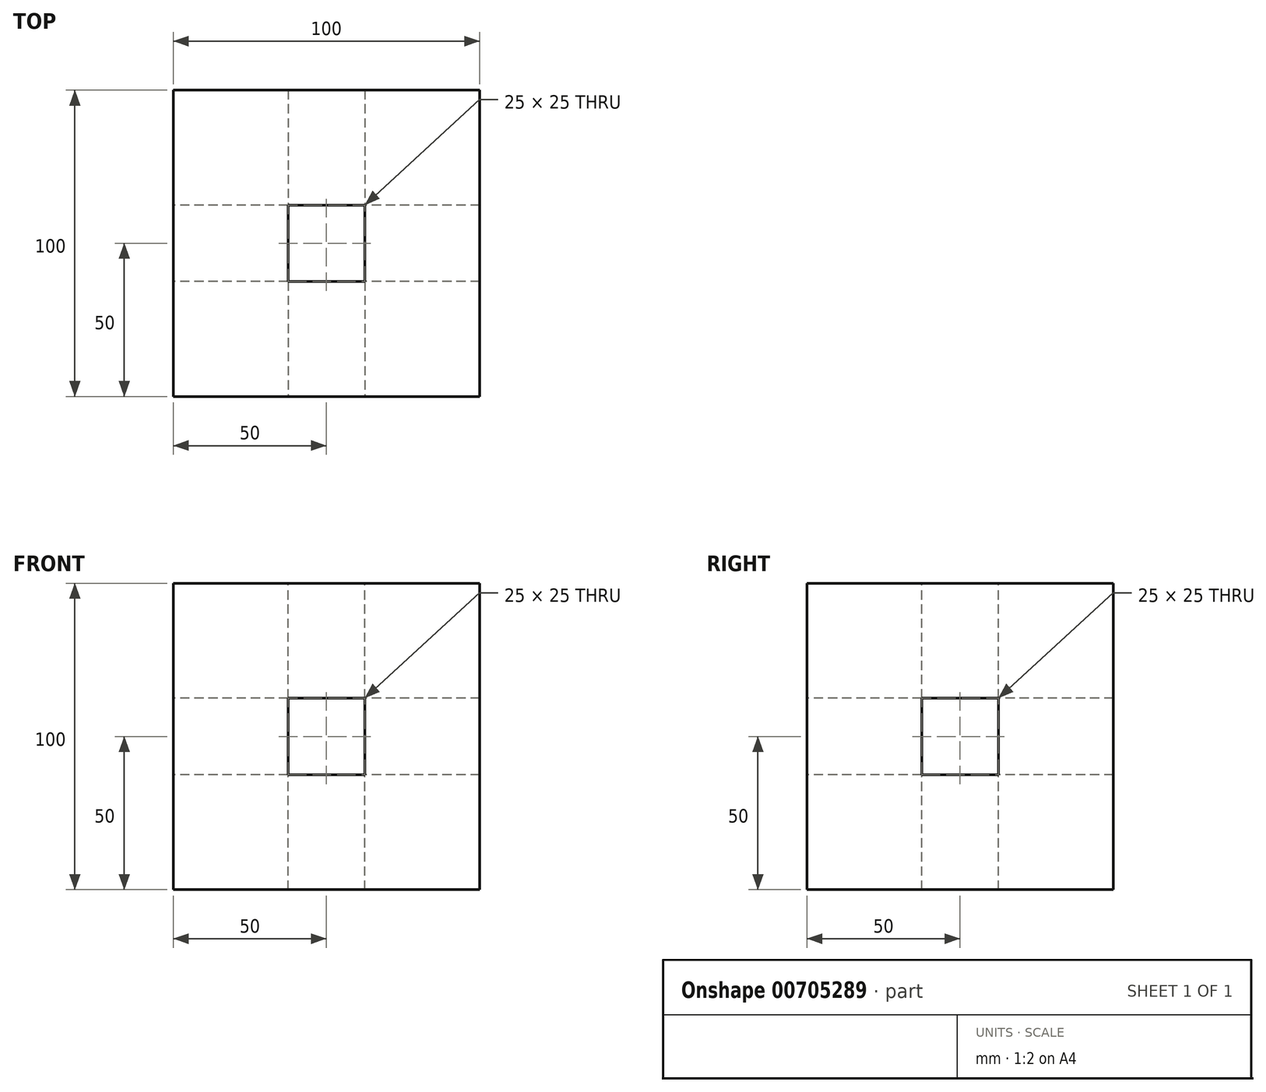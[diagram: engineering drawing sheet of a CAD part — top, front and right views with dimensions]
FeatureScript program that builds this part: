
annotation { "Feature Type Name" : "Feature", "Feature Type Description" : "" }
export const myFeature = defineFeature(function(context is Context, id is Id, definition is map)
    precondition{}
    {
        {
            var Q0;
            Q0=qCreatedBy(makeId("Top.planeOp"),FACE);
            var sketch = newSketch(context, id + "F0", { "sketchPlane" : qUnion([Q0])});
            skLineSegment(sketch, "E0.bottom", {"start": v(50, -50) * mm, "end": v(-50, -50) * mm});
            skLineSegment(sketch, "E0.top", {"start": v(50, 50) * mm, "end": v(-50, 50) * mm});
            skLineSegment(sketch, "E0.left", {"start": v(50, -50) * mm, "end": v(50, 50) * mm});
            skLineSegment(sketch, "E0.right", {"start": v(-50, -50) * mm, "end": v(-50, 50) * mm});
            skPoint(sketch, "E0.middle", {"position": v(0, 0) * mm});
            skSolve(sketch);
        }
        {
            var Q0;
            Q0=qSketchRegion(id+"F0",true);
            extrude(context, id + "F1", {"entities" : qUnion([Q0]), "depth" : 100 * mm, "offsetDistance" : 25 * mm});
        }
        {
            var Q0;
            Q0=makeQuery(id+"F1.opExtrude","SWEPT_FACE",FACE,{"disambiguationData":[OSD([sQuery(id+"F0.wireOp",EDGE,"E0.bottom")])]});
            var sketch = newSketch(context, id + "F2", { "sketchPlane" : qUnion([Q0])});
            skLineSegment(sketch, "E1.bottom", {"start": v(12.5, 37.5) * mm, "end": v(-12.5, 37.5) * mm});
            skLineSegment(sketch, "E1.top", {"start": v(12.5, 62.5) * mm, "end": v(-12.5, 62.5) * mm});
            skLineSegment(sketch, "E1.left", {"start": v(12.5, 37.5) * mm, "end": v(12.5, 62.5) * mm});
            skLineSegment(sketch, "E1.right", {"start": v(-12.5, 37.5) * mm, "end": v(-12.5, 62.5) * mm});
            skPoint(sketch, "E1.middle", {"position": v(0, 50) * mm});
            skPoint(sketch, "E1.middle.positionSnap0", {"position": v(-50, 50) * mm});
            skPoint(sketch, "E1.centerSnap0", {"position": v(-50, 50) * mm});
            skSolve(sketch);
        }
        {
            var Q0;
            Q0=makeQuery(id+"F2.imprint","IMPRINT",FACE,{"disambiguationData":[TD([[makeQuery(id+"F2.imprint","IMPRINT",EDGE,{"derivedFrom":sQuery(id+"F2.wireOp",EDGE,"E1.bottom")}),-1.0]])]});
            extrude(context, id + "F3", {"entities" : qUnion([Q0]), "operationType" : NewBodyOperationType.REMOVE, "endBound" : BoundingType.THROUGH_ALL, "oppositeDirection" : true, "depth" : 25 * mm, "offsetDistance" : 25 * mm});
        }
        {
            var Q0;
            Q0=makeQuery(id+"F1.opExtrude","SWEPT_FACE",FACE,{"disambiguationData":[OSD([sQuery(id+"F0.wireOp",EDGE,"E0.right")])]});
            var sketch = newSketch(context, id + "F4", { "sketchPlane" : qUnion([Q0])});
            skLineSegment(sketch, "E2.bottom", {"start": v(12.5, 37.5) * mm, "end": v(-12.5, 37.5) * mm});
            skLineSegment(sketch, "E2.top", {"start": v(12.5, 62.5) * mm, "end": v(-12.5, 62.5) * mm});
            skLineSegment(sketch, "E2.left", {"start": v(12.5, 37.5) * mm, "end": v(12.5, 62.5) * mm});
            skLineSegment(sketch, "E2.right", {"start": v(-12.5, 37.5) * mm, "end": v(-12.5, 62.5) * mm});
            skPoint(sketch, "E2.middle", {"position": v(0, 50) * mm});
            skPoint(sketch, "E2.middle.positionSnap0", {"position": v(50, 50) * mm});
            skPoint(sketch, "E2.centerSnap0", {"position": v(50, 50) * mm});
            skSolve(sketch);
        }
        {
            var Q0;
            Q0=qSketchRegion(id+"F4",true);
            extrude(context, id + "F5", {"entities" : qUnion([Q0]), "operationType" : NewBodyOperationType.REMOVE, "endBound" : BoundingType.THROUGH_ALL, "oppositeDirection" : true, "depth" : 25 * mm, "offsetDistance" : 25 * mm});
        }
        {
            var Q0;
            Q0=makeQuery(id+"F1.opExtrude","CAP_FACE",FACE,{"disambiguationData":[OSD([sQuery(id+"F0.wireOp",EDGE,"E0.bottom"),sQuery(id+"F0.wireOp",EDGE,"E0.top"),sQuery(id+"F0.wireOp",EDGE,"E0.left"),sQuery(id+"F0.wireOp",EDGE,"E0.right")])],"isStart":false});
            var sketch = newSketch(context, id + "F6", { "sketchPlane" : qUnion([Q0])});
            skLineSegment(sketch, "E3.bottom", {"start": v(12.5, -12.5) * mm, "end": v(-12.5, -12.5) * mm});
            skLineSegment(sketch, "E3.top", {"start": v(12.5, 12.5) * mm, "end": v(-12.5, 12.5) * mm});
            skLineSegment(sketch, "E3.left", {"start": v(12.5, -12.5) * mm, "end": v(12.5, 12.5) * mm});
            skLineSegment(sketch, "E3.right", {"start": v(-12.5, -12.5) * mm, "end": v(-12.5, 12.5) * mm});
            skPoint(sketch, "E3.middle", {"position": v(0, 0) * mm});
            skSolve(sketch);
        }
        {
            var Q0;
            Q0=makeQuery(id+"F6.imprint","IMPRINT",FACE,{"disambiguationData":[TD([[makeQuery(id+"F6.imprint","IMPRINT",EDGE,{"derivedFrom":sQuery(id+"F6.wireOp",EDGE,"E3.bottom")}),-1.0]])]});
            extrude(context, id + "F7", {"entities" : qUnion([Q0]), "operationType" : NewBodyOperationType.REMOVE, "endBound" : BoundingType.THROUGH_ALL, "oppositeDirection" : true, "depth" : 25 * mm, "offsetDistance" : 25 * mm});
        }
    });
